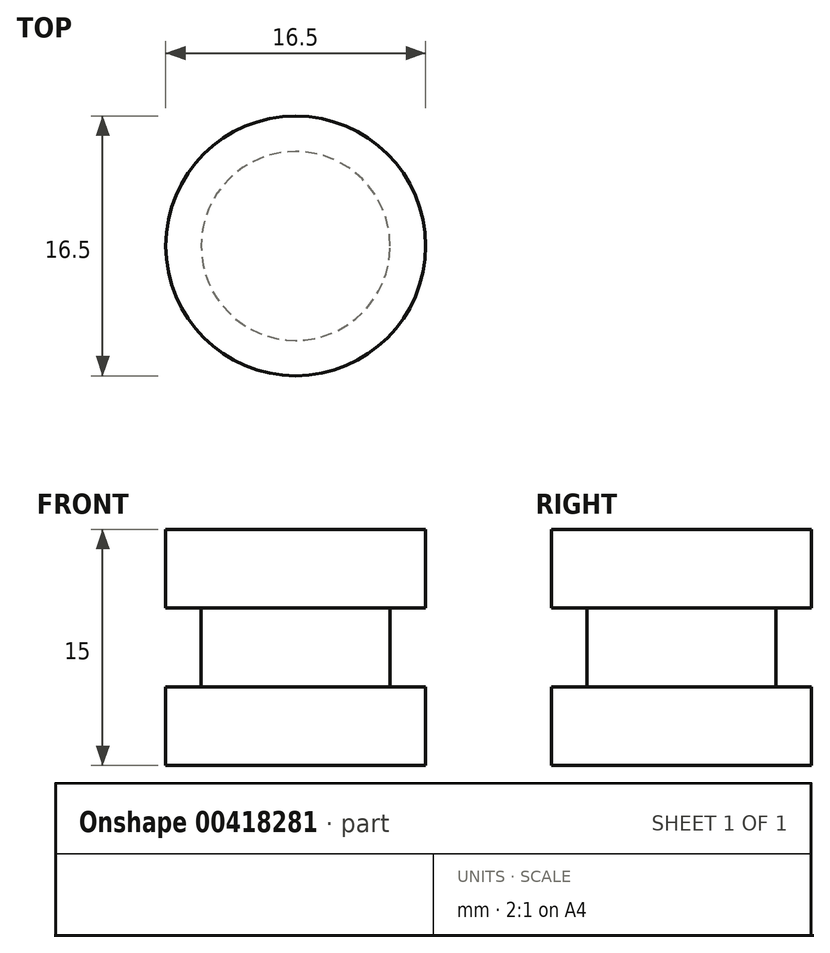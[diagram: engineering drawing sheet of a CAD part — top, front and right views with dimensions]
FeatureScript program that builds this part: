
annotation { "Feature Type Name" : "Feature", "Feature Type Description" : "" }
export const myFeature = defineFeature(function(context is Context, id is Id, definition is map)
    precondition{}
    {
        {
            var Q0;
            Q0=qCreatedBy(makeId("Top.planeOp"),FACE);
            var sketch = newSketch(context, id + "F0", { "sketchPlane" : qUnion([Q0])});
            skCircle(sketch, "E0", {"center": v(0, 0) * mm, "radius": 8.25 * mm});
            skSolve(sketch);
        }
        {
            var Q0;
            Q0 = qSketchRegion(id + "F0", true);
            extrude(context, id + "F1", {"entities" : qUnion([Q0]), "oppositeDirection" : true, "depth" : 5 * mm, "offsetDistance" : 25 * mm});
        }
        {
            var Q0;
            Q0=qCreatedBy(makeId("Top.planeOp"),FACE);
            var sketch = newSketch(context, id + "F2", { "sketchPlane" : qUnion([Q0])});
            skCircle(sketch, "E1", {"center": v(0, 0) * mm, "radius": 6 * mm});
            skSolve(sketch);
        }
        {
            var Q0;
            Q0 = qSketchRegion(id + "F2", true);
            extrude(context, id + "F3", {"entities" : qUnion([Q0]), "operationType" : NewBodyOperationType.ADD, "depth" : 5 * mm, "offsetDistance" : 25 * mm});
        }
        {
            var Q0;
            Q0=makeQuery(id+"F3.opExtrude","CAP_FACE",FACE,{"disambiguationData":[OSD([sQuery(id+"F2.wireOp",EDGE,"E1")])],"isStart":false});
            var sketch = newSketch(context, id + "F4", { "sketchPlane" : qUnion([Q0])});
            skCircle(sketch, "E2", {"center": v(0, 0) * mm, "radius": 8.25 * mm});
            skSolve(sketch);
        }
        {
            var Q0;
            Q0 = qSketchRegion(id + "F4", true);
            extrude(context, id + "F5", {"entities" : qUnion([Q0]), "operationType" : NewBodyOperationType.ADD, "depth" : 5 * mm, "offsetDistance" : 25 * mm});
        }
    });
